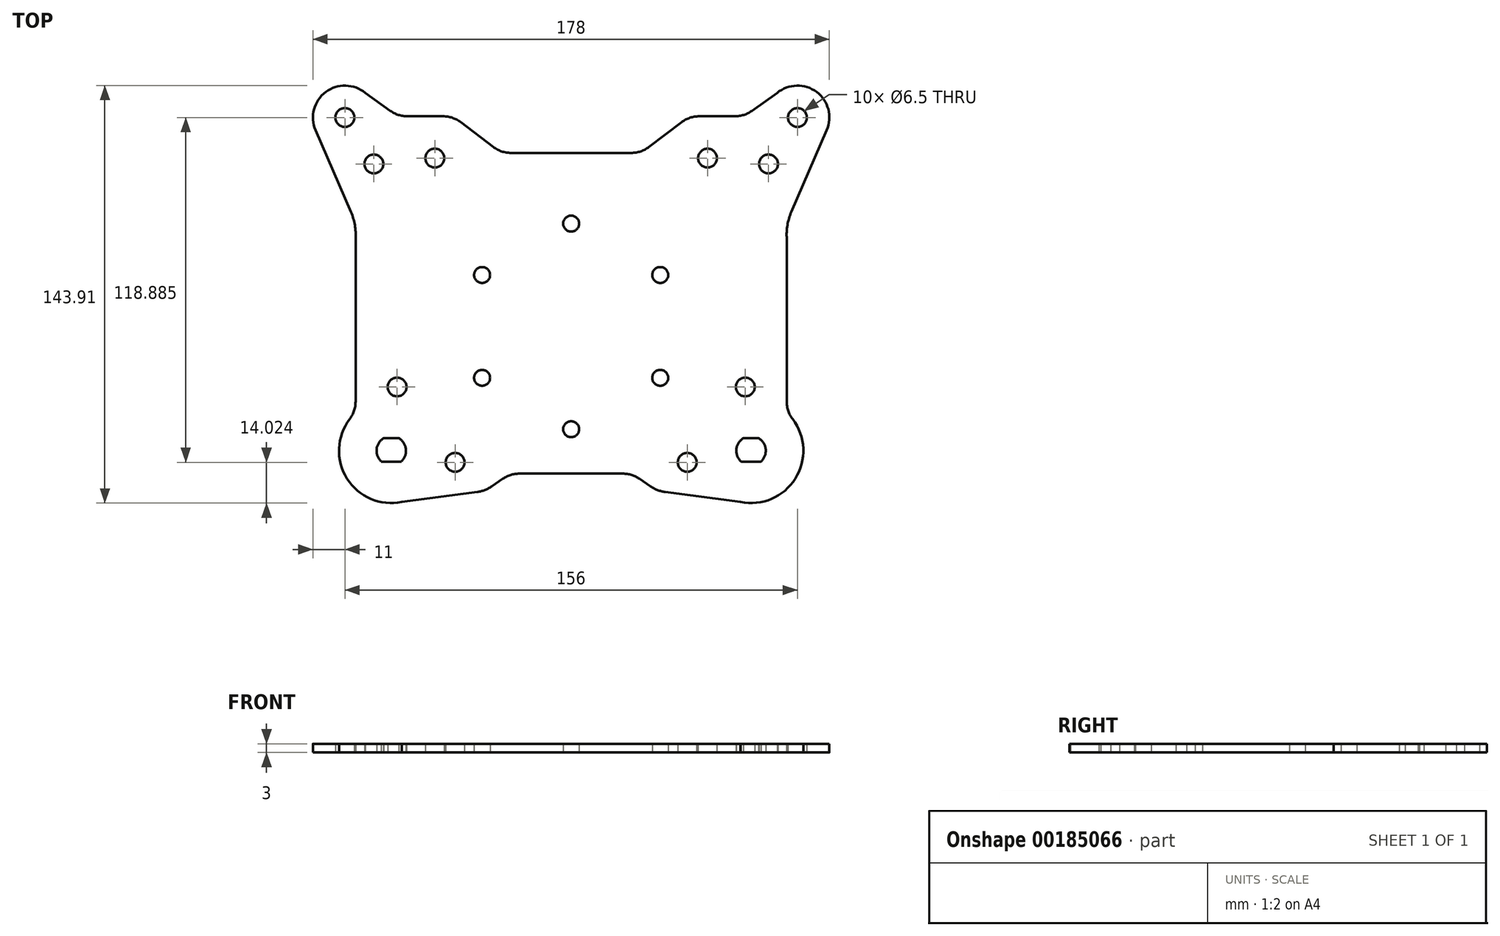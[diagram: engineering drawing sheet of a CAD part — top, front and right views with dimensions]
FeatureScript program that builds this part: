
annotation { "Feature Type Name" : "Feature", "Feature Type Description" : "" }
export const myFeature = defineFeature(function(context is Context, id is Id, definition is map)
    precondition{}
    {
        {
            var Q0;
            Q0=qCreatedBy(makeId("Top.planeOp"),FACE);
            var sketch = newSketch(context, id + "F0", { "sketchPlane" : qUnion([Q0])});
            skPoint(sketch, "E0.middle", {"position": v(0, 0) * mm});
            skCircle(sketch, "E1.3.0", {"center": v(0, -60.17) * mm, "radius": 2.75 * mm});
            skCircle(sketch, "E1.4.0", {"center": v(30.7, -42.45) * mm, "radius": 2.75 * mm});
            skCircle(sketch, "E1.5.0", {"center": v(30.7, -7) * mm, "radius": 2.75 * mm});
            skCircle(sketch, "E2", {"center": v(47, 33.29) * mm, "radius": 3.25 * mm});
            skCircle(sketch, "E3", {"center": v(68, 31.29) * mm, "radius": 3.25 * mm});
            skCircle(sketch, "E4", {"center": v(78, 47.29) * mm, "radius": 3.25 * mm});
            skCircle(sketch, "E5", {"center": v(40, -71.6) * mm, "radius": 3.25 * mm});
            skCircle(sketch, "E6", {"center": v(60, -45.6) * mm, "radius": 3.25 * mm});
            skArc(sketch, "E7", {"start": v(59.39, -63.24) * mm, "mid": v(56.95, -67.07) * mm, "end": v(58.54, -71.31) * mm});
            skArc(sketch, "E8", {"start": v(58.36, -85.25) * mm, "mid": v(77.25, -77.2) * mm, "end": v(76.35, -56.68) * mm});
            skArc(sketch, "E9", {"start": v(88.1, 42.92) * mm, "mid": v(84.6, 56.09) * mm, "end": v(70.98, 55.76) * mm});
            skLineSegment(sketch, "E10", {"start": v(75.9, 14.73) * mm, "end": v(88.1, 42.92) * mm});
            skLineSegment(sketch, "E11", {"start": v(70.98, 55.76) * mm, "end": v(62.25, 49.56) * mm});
            skLineSegment(sketch, "E12", {"start": v(56.46, 47.71) * mm, "end": v(44.12, 47.71) * mm});
            skLineSegment(sketch, "E13", {"start": v(38.08, 45.68) * mm, "end": v(26.77, 37.11) * mm});
            skLineSegment(sketch, "E14", {"start": v(20.73, 35.08) * mm, "end": v(0, 35.08) * mm});
            skLineSegment(sketch, "E15", {"start": v(58.36, -85.25) * mm, "end": v(32.38, -81.8) * mm});
            skLineSegment(sketch, "E16", {"start": v(27.35, -79.87) * mm, "end": v(23.53, -77.25) * mm});
            skLineSegment(sketch, "E17", {"start": v(17.86, -75.49) * mm, "end": v(0, -75.49) * mm});
            skPoint(sketch, "E18.visualSharp", {"position": v(24.1, 35.08) * mm});
            skArc(sketch, "E18.filletArc", {"start": v(20.73, 35.08) * mm, "mid": v(23.92, 35.6) * mm, "end": v(26.77, 37.11) * mm});
            skPoint(sketch, "E19.visualSharp", {"position": v(59.65, 47.71) * mm});
            skArc(sketch, "E19.filletArc", {"start": v(56.46, 47.71) * mm, "mid": v(59.5, 48.19) * mm, "end": v(62.25, 49.56) * mm});
            skPoint(sketch, "E20.visualSharp", {"position": v(40.76, 47.71) * mm});
            skArc(sketch, "E20.filletArc", {"start": v(44.12, 47.71) * mm, "mid": v(40.93, 47.2) * mm, "end": v(38.08, 45.68) * mm});
            skPoint(sketch, "E21.visualSharp", {"position": v(73.97, 10.28) * mm});
            skArc(sketch, "E21.filletArc", {"start": v(75.9, 14.73) * mm, "mid": v(74.55, 10.18) * mm, "end": v(74.3, 5.45) * mm});
            skPoint(sketch, "E22.visualSharp", {"position": v(29.63, -81.44) * mm});
            skArc(sketch, "E22.filletArc", {"start": v(27.35, -79.87) * mm, "mid": v(29.75, -81.14) * mm, "end": v(32.38, -81.8) * mm});
            skPoint(sketch, "E23.visualSharp", {"position": v(20.97, -75.49) * mm});
            skArc(sketch, "E23.filletArc", {"start": v(23.53, -77.25) * mm, "mid": v(20.83, -75.94) * mm, "end": v(17.86, -75.49) * mm});
            skLineSegment(sketch, "E24", {"start": v(74.3, 5.45) * mm, "end": v(74.3, -50.63) * mm});
            skPoint(sketch, "E25.visualSharp", {"position": v(74.3, -54.43) * mm});
            skArc(sketch, "E25.filletArc", {"start": v(74.3, -50.63) * mm, "mid": v(74.83, -53.83) * mm, "end": v(76.35, -56.68) * mm});
            skArc(sketch, "E26.MirrorCS", {"start": v(-23.53, -77.25) * mm, "mid": v(-20.83, -75.94) * mm, "end": v(-17.86, -75.49) * mm});
            skArc(sketch, "E27.MirrorCS", {"start": v(-56.46, 47.71) * mm, "mid": v(-59.5, 48.19) * mm, "end": v(-62.25, 49.56) * mm});
            skArc(sketch, "E28.MirrorCS", {"start": v(-44.12, 47.71) * mm, "mid": v(-40.93, 47.2) * mm, "end": v(-38.08, 45.68) * mm});
            skArc(sketch, "E29.MirrorCS", {"start": v(-27.35, -79.87) * mm, "mid": v(-29.75, -81.14) * mm, "end": v(-32.38, -81.8) * mm});
            skArc(sketch, "E30.MirrorCS", {"start": v(-20.73, 35.08) * mm, "mid": v(-23.92, 35.6) * mm, "end": v(-26.77, 37.11) * mm});
            skArc(sketch, "E31.MirrorCS", {"start": v(-74.3, -50.63) * mm, "mid": v(-74.83, -53.83) * mm, "end": v(-76.35, -56.68) * mm});
            skLineSegment(sketch, "E32.MirrorCS", {"start": v(-27.35, -79.87) * mm, "end": v(-23.53, -77.25) * mm});
            skArc(sketch, "E33.MirrorCS", {"start": v(-75.9, 14.73) * mm, "mid": v(-74.55, 10.18) * mm, "end": v(-74.3, 5.45) * mm});
            skLineSegment(sketch, "E34.MirrorCS", {"start": v(-17.86, -75.49) * mm, "end": v(0, -75.49) * mm});
            skArc(sketch, "E35.MirrorCS", {"start": v(-58.36, -85.25) * mm, "mid": v(-77.25, -77.2) * mm, "end": v(-76.35, -56.68) * mm});
            skPoint(sketch, "E36.MirrorP", {"position": v(-74.3, -54.43) * mm});
            skCircle(sketch, "E37.MirrorC", {"center": v(-30.7, -7) * mm, "radius": 2.75 * mm});
            skArc(sketch, "E38.MirrorCS", {"start": v(-88.1, 42.92) * mm, "mid": v(-84.6, 56.09) * mm, "end": v(-70.98, 55.76) * mm});
            skCircle(sketch, "E39.MirrorC", {"center": v(-60, -45.6) * mm, "radius": 3.25 * mm});
            skLineSegment(sketch, "E40.MirrorCS", {"start": v(-38.08, 45.68) * mm, "end": v(-26.77, 37.11) * mm});
            skPoint(sketch, "E41.MirrorP", {"position": v(-24.1, 35.08) * mm});
            skLineSegment(sketch, "E42.MirrorCS", {"start": v(-58.36, -85.25) * mm, "end": v(-32.38, -81.8) * mm});
            skLineSegment(sketch, "E43.MirrorCS", {"start": v(-74.3, 5.45) * mm, "end": v(-74.3, -50.63) * mm});
            skCircle(sketch, "E44.MirrorC", {"center": v(-78, 47.29) * mm, "radius": 3.25 * mm});
            skCircle(sketch, "E45.MirrorC", {"center": v(-68, 31.29) * mm, "radius": 3.25 * mm});
            skCircle(sketch, "E46.MirrorC", {"center": v(-40, -71.6) * mm, "radius": 3.25 * mm});
            skCircle(sketch, "E47.MirrorC", {"center": v(-47, 33.29) * mm, "radius": 3.25 * mm});
            skCircle(sketch, "E48.MirrorC", {"center": v(-30.7, -42.45) * mm, "radius": 2.75 * mm});
            skCircle(sketch, "E49.MirrorC", {"center": v(0, 10.72) * mm, "radius": 2.75 * mm});
            skPoint(sketch, "E50.MirrorP", {"position": v(-59.65, 47.71) * mm});
            skLineSegment(sketch, "E51.MirrorCS", {"start": v(-56.46, 47.71) * mm, "end": v(-44.12, 47.71) * mm});
            skPoint(sketch, "E52.MirrorP", {"position": v(-40.76, 47.71) * mm});
            skLineSegment(sketch, "E53.MirrorCS", {"start": v(-70.98, 55.76) * mm, "end": v(-62.25, 49.56) * mm});
            skLineSegment(sketch, "E54.MirrorCS", {"start": v(-20.73, 35.08) * mm, "end": v(0, 35.08) * mm});
            skLineSegment(sketch, "E55.MirrorCS", {"start": v(-75.9, 14.73) * mm, "end": v(-88.1, 42.92) * mm});
            skPoint(sketch, "E56.MirrorP", {"position": v(-73.97, 10.28) * mm});
            skPoint(sketch, "E57.MirrorP", {"position": v(-29.63, -81.44) * mm});
            skPoint(sketch, "E58.MirrorP", {"position": v(-20.97, -75.49) * mm});
            skLineSegment(sketch, "E59.bottom", {"start": v(64.61, -63.24) * mm, "end": v(59.39, -63.24) * mm});
            skLineSegment(sketch, "E59.top", {"start": v(65.46, -71.31) * mm, "end": v(58.54, -71.31) * mm});
            skArc(sketch, "E60.trimOffspring", {"start": v(65.46, -71.31) * mm, "mid": v(67.05, -67.07) * mm, "end": v(64.61, -63.24) * mm});
            skLineSegment(sketch, "E61.MirrorCS", {"start": v(-64.61, -63.24) * mm, "end": v(-59.39, -63.24) * mm});
            skLineSegment(sketch, "E62.MirrorCS", {"start": v(-65.46, -71.31) * mm, "end": v(-58.54, -71.31) * mm});
            skArc(sketch, "E63.MirrorCS", {"start": v(-59.39, -63.24) * mm, "mid": v(-56.95, -67.07) * mm, "end": v(-58.54, -71.31) * mm});
            skArc(sketch, "E64.MirrorCS", {"start": v(-65.46, -71.31) * mm, "mid": v(-67.05, -67.07) * mm, "end": v(-64.61, -63.24) * mm});
            skSolve(sketch);
        }
        {
            var Q0;
            Q0=makeQuery(id+"F0.imprint","IMPRINT",FACE,{"disambiguationData":[TD([[makeQuery(id+"F0.imprint","IMPRINT",EDGE,{"derivedFrom":sQuery(id+"F0.wireOp",EDGE,"E1.4.0")}),-1.0]])]});
            extrude(context, id + "F1", {"entities" : qUnion([Q0]), "depth" : 3 * mm});
        }
    });
